# Revit family: DA02280000
name_source: partatom
category: Apparecchi idraulici
units: mm (PartAtom-declared; Revit-internal decimal feet)

## family parameters
Basato su piano di lavoro = No
Condiviso = No
Numero OmniClass = 23.45.00.00
Punto di calcolo locali = No
Quota connettore circolare = Usa diametro
Sempre verticale = Sì
Taglio con vuoti quando caricato = No
Tipo di parte = Normale
Titolo OmniClass = Sanitary, Laundry, and Cleaning Equipment

## types (1)
- DA02280000
    Commenti sul tipo = Realizzato in ottemperanza ai requisiti gestionali della norma EN ISO 9001. Collaudato al 100% secondo la normativa EN 12266-1
    Descrizione = Utilizzato per la filtrazione degli impianti di riscaldamento, idrici, igienico-sanitari, aria compressa e in generale con ogni fluido non corrosivo
    Materiale = Prodotto in lega di ottone “CR” – “DZR" conforme alla norma EN 12165-CW511L-M nelle misure fino a 1"1/2 e alla norma EN 1982-CB770S Pb 0,2% max nelle misure da 2"
    Modello = Cim 74ACRNL/2
    Pressione nominale = PN 20
    Produttore = CIMBERIO SPA
    Prospetto di default = 0 mm  [stored 0 ft]
    Temperatura di esercizio = -10 ÷ 150°C
    URL = https://web.cimberio.com

note: [stored X ft] marks values corroborated as IEEE doubles in the binary element streams (Revit-internal decimal feet)
